# Revit family: Deca_Misturador Termostato Decaterm_2430.C.034GGGGGG
name_source: partatom
category: Plumbing Fixtures
revit_build: Autodesk Revit Architecture 2012 (Build: 20120126_0600(x64)
units: mm (PartAtom-declared; Revit-internal decimal feet)

## types (2) — shared parameters
Aprovado por = Contino/quattroD
Atendimento ao Cliente = 0800-0117073
Consumo = Varia com a pressão
Criado por = Contino/quattroD
Description = Misturador termostático
Diâmetro Saída Água = 20 mm  [stored 0.0656168 ft]
Diâmetro Água Fria = 15 mm  [stored 0.0492126 ft]
Diâmetro Água Quente = 15 mm  [stored 0.0492126 ft]
Flow Pressure = 0.00 psi
Linha = Decaterm
Louça/Metais = Metal
Manufacturer = Deca
Material = Deca_Latão Cromado e Plástico de Engenharia
Peso Liquido (Kg) = 2.7
Pressão = 2 A 40 mca
Produto = Misturador Termostato Decaterm
Raio Saída Água = 10 mm  [stored 0.0328084 ft]
Raio Água Fria = 8 mm  [stored 0.0262467 ft]
Raio Água Quente = 8 mm  [stored 0.0262467 ft]
Segmento = Luxo
URL = www.deca.com.br/produtos
Variações de COR = Cromado (2430.C.034); Dourado (2430.D.034)
zero-valued in all types: CWFU, HWFU

## per-type parameters (varying)
| type | Assembly Code | Código | Default Elevation | Misturador | Model |
| 2430.C.034_Cromado CR10 | D2020 | 2430.C.034 | 1000 mm  [stored 3.28084 ft] | Deca CR10 Cromado Metal | 2430.C.034 |
| 2430.D.034_Dourado DR11 | D2010710 | 2430.D.034 | 0 mm  [stored 0 ft] | Deca DR11 Dourado Metal | 2430.D.034 |

note: [stored X ft] marks values corroborated as IEEE doubles in the binary element streams (Revit-internal decimal feet)

## geometry (parser evidence)
native form markers: Blend x2, Sweep x1
no freeform markers — native parametric forms only
